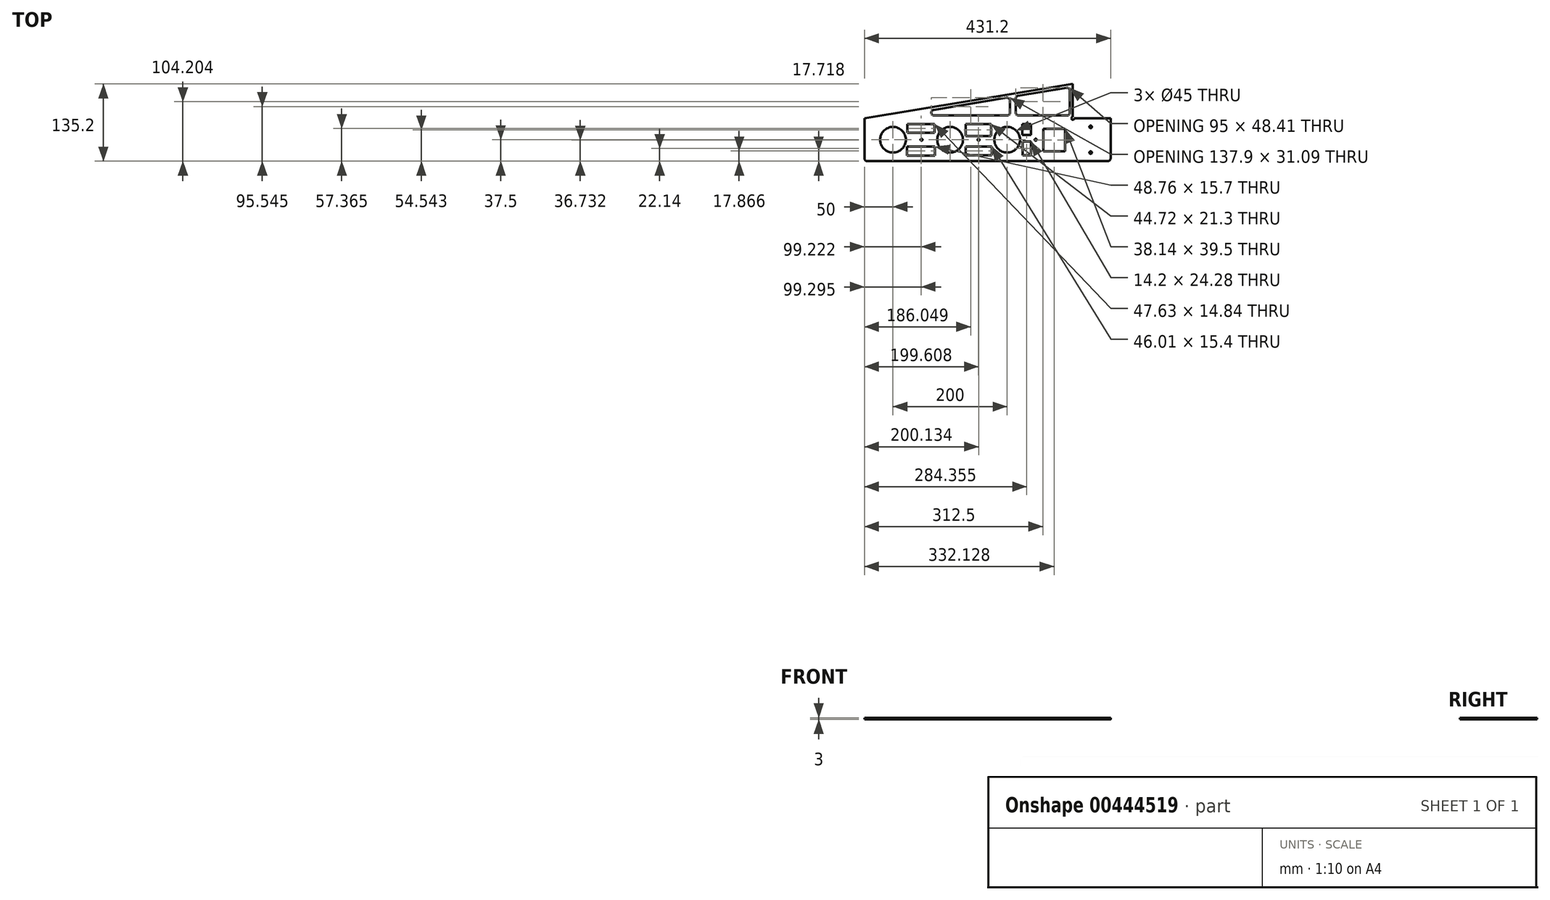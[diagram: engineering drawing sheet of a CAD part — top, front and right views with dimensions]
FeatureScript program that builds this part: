
annotation { "Feature Type Name" : "Feature", "Feature Type Description" : "" }
export const myFeature = defineFeature(function(context is Context, id is Id, definition is map)
    precondition{}
    {
        {
            var Q0;
            Q0=qCreatedBy(makeId("Top.planeOp"),FACE);
            var sketch = newSketch(context, id + "F0", { "sketchPlane" : qUnion([Q0])});
            skLineSegment(sketch, "E0.bottom", {"start": v(5, 0) * mm, "end": v(426.2, 0) * mm});
            skLineSegment(sketch, "E0.top", {"start": v(0, 75) * mm, "end": v(431.2, 75) * mm});
            skLineSegment(sketch, "E0.left", {"start": v(0, 5) * mm, "end": v(0, 75) * mm});
            skLineSegment(sketch, "E0.right", {"start": v(431.2, 5) * mm, "end": v(431.2, 75) * mm});
            skLineSegment(sketch, "E1", {"start": v(0, 75) * mm, "end": v(365, 135.2) * mm});
            skLineSegment(sketch, "E2", {"start": v(365, 135.2) * mm, "end": v(365, 75) * mm});
            skPoint(sketch, "E2.endSnap0", {"position": v(215.6, 75) * mm});
            skCircle(sketch, "E3", {"center": v(365, 75) * mm, "radius": 2.5 * mm});
            skCircle(sketch, "E4", {"center": v(100, 37.5) * mm, "radius": 1.75 * mm});
            skPoint(sketch, "E4.centerSnap0", {"position": v(0, 37.5) * mm});
            skCircle(sketch, "E5", {"center": v(200, 37.5) * mm, "radius": 1.75 * mm});
            skCircle(sketch, "E6", {"center": v(300, 37.5) * mm, "radius": 1.75 * mm});
            skCircle(sketch, "E7", {"center": v(396.2, 60) * mm, "radius": 2.25 * mm});
            skCircle(sketch, "E8", {"center": v(396.2, 15) * mm, "radius": 2.25 * mm});
            skLineSegment(sketch, "E9.0", {"start": v(360, 123.42) * mm, "end": v(360, 85) * mm});
            skLineSegment(sketch, "E10.0", {"start": v(122.08, 80) * mm, "end": v(250, 80) * mm});
            skLineSegment(sketch, "E10.1", {"start": v(121.27, 89.93) * mm, "end": v(249.19, 111.03) * mm});
            skPoint(sketch, "E11.visualSharp", {"position": v(360, 129.3) * mm});
            skArc(sketch, "E11.filletArc", {"start": v(360, 123.42) * mm, "mid": v(358.24, 127.23) * mm, "end": v(354.19, 128.35) * mm});
            skArc(sketch, "E12.filletArc", {"start": v(355, 80) * mm, "mid": v(358.54, 81.46) * mm, "end": v(360, 85) * mm});
            skPoint(sketch, "E13.visualSharp", {"position": v(61.04, 80) * mm});
            skArc(sketch, "E13.filletArc", {"start": v(121.27, 89.93) * mm, "mid": v(117.1, 84.6) * mm, "end": v(122.08, 80) * mm});
            skLineSegment(sketch, "E14.0", {"start": v(265, 85) * mm, "end": v(265, 109.4) * mm});
            skLineSegment(sketch, "E15.0", {"start": v(255, 85) * mm, "end": v(255, 106.1) * mm});
            skLineSegment(sketch, "E16.trimOffspring", {"start": v(270, 80) * mm, "end": v(355, 80) * mm});
            skLineSegment(sketch, "E17.trimOffspring", {"start": v(269.19, 114.33) * mm, "end": v(354.19, 128.35) * mm});
            skPoint(sketch, "E18.visualSharp", {"position": v(255, 111.99) * mm});
            skArc(sketch, "E18.filletArc", {"start": v(255, 106.1) * mm, "mid": v(253.24, 109.91) * mm, "end": v(249.19, 111.03) * mm});
            skPoint(sketch, "E19.visualSharp", {"position": v(255, 80) * mm});
            skArc(sketch, "E19.filletArc", {"start": v(250, 80) * mm, "mid": v(253.54, 81.46) * mm, "end": v(255, 85) * mm});
            skPoint(sketch, "E20.visualSharp", {"position": v(265, 113.64) * mm});
            skArc(sketch, "E20.filletArc", {"start": v(269.19, 114.33) * mm, "mid": v(266.19, 112.63) * mm, "end": v(265, 109.4) * mm});
            skPoint(sketch, "E21.visualSharp", {"position": v(265, 80) * mm});
            skArc(sketch, "E21.filletArc", {"start": v(265, 85) * mm, "mid": v(266.46, 81.46) * mm, "end": v(270, 80) * mm});
            skCircle(sketch, "E22", {"center": v(50, 37.5) * mm, "radius": 22.5 * mm});
            skCircle(sketch, "E23.1.0.0", {"center": v(150, 37.5) * mm, "radius": 22.5 * mm});
            skCircle(sketch, "E23.2.0.0", {"center": v(250, 37.5) * mm, "radius": 22.5 * mm});
            skLineSegment(sketch, "E23.direction1", {"start": v(50, 37.5) * mm, "end": v(150, 37.5) * mm, "construction": true});
            skPoint(sketch, "E24.visualSharp", {"position": v(0, 0) * mm});
            skArc(sketch, "E24.filletArc", {"start": v(0, 5) * mm, "mid": v(1.46, 1.46) * mm, "end": v(5, 0) * mm});
            skPoint(sketch, "E25.visualSharp", {"position": v(431.2, 0) * mm});
            skArc(sketch, "E25.filletArc", {"start": v(426.2, 0) * mm, "mid": v(429.74, 1.46) * mm, "end": v(431.2, 5) * mm});
            skLineSegment(sketch, "E26.0", {"start": v(10, 15) * mm, "end": v(10, 60) * mm});
            skLineSegment(sketch, "E27.0", {"start": v(15, 10) * mm, "end": v(346.2, 10) * mm});
            skLineSegment(sketch, "E28.0", {"start": v(351.2, 15) * mm, "end": v(351.2, 60) * mm});
            skLineSegment(sketch, "E29.0", {"start": v(15, 65) * mm, "end": v(346.2, 65) * mm});
            skPoint(sketch, "E30.visualSharp", {"position": v(10, 10) * mm});
            skArc(sketch, "E30.filletArc", {"start": v(10, 15) * mm, "mid": v(11.46, 11.46) * mm, "end": v(15, 10) * mm});
            skPoint(sketch, "E31.visualSharp", {"position": v(10, 65) * mm});
            skArc(sketch, "E31.filletArc", {"start": v(15, 65) * mm, "mid": v(11.46, 63.54) * mm, "end": v(10, 60) * mm});
            skPoint(sketch, "E32.visualSharp", {"position": v(351.2, 65) * mm});
            skArc(sketch, "E32.filletArc", {"start": v(351.2, 60) * mm, "mid": v(349.74, 63.54) * mm, "end": v(346.2, 65) * mm});
            skPoint(sketch, "E33.visualSharp", {"position": v(351.2, 10) * mm});
            skArc(sketch, "E33.filletArc", {"start": v(346.2, 10) * mm, "mid": v(349.74, 11.46) * mm, "end": v(351.2, 15) * mm});
            skLineSegment(sketch, "E34.bottom", {"start": v(74.84, 9.87) * mm, "end": v(123.6, 9.87) * mm});
            skLineSegment(sketch, "E34.top", {"start": v(74.84, 25.57) * mm, "end": v(123.6, 25.57) * mm});
            skLineSegment(sketch, "E34.left", {"start": v(74.84, 9.87) * mm, "end": v(74.84, 25.57) * mm});
            skLineSegment(sketch, "E34.right", {"start": v(123.6, 9.87) * mm, "end": v(123.6, 25.57) * mm});
            skLineSegment(sketch, "E35.bottom", {"start": v(177.13, 10.17) * mm, "end": v(223.14, 10.17) * mm});
            skLineSegment(sketch, "E35.top", {"start": v(177.13, 25.57) * mm, "end": v(223.14, 25.57) * mm});
            skLineSegment(sketch, "E35.left", {"start": v(177.13, 10.17) * mm, "end": v(177.13, 25.57) * mm});
            skLineSegment(sketch, "E35.right", {"start": v(223.14, 10.17) * mm, "end": v(223.14, 25.57) * mm});
            skLineSegment(sketch, "E36.bottom", {"start": v(75.48, 64.79) * mm, "end": v(123.11, 64.79) * mm});
            skLineSegment(sketch, "E36.top", {"start": v(75.48, 49.94) * mm, "end": v(123.11, 49.94) * mm});
            skLineSegment(sketch, "E36.left", {"start": v(75.48, 64.79) * mm, "end": v(75.48, 49.94) * mm});
            skLineSegment(sketch, "E36.right", {"start": v(123.11, 64.79) * mm, "end": v(123.11, 49.94) * mm});
            skLineSegment(sketch, "E37.bottom", {"start": v(177.25, 43.9) * mm, "end": v(221.97, 43.9) * mm});
            skLineSegment(sketch, "E37.top", {"start": v(177.25, 65.2) * mm, "end": v(221.97, 65.2) * mm});
            skLineSegment(sketch, "E37.left", {"start": v(177.25, 43.9) * mm, "end": v(177.25, 65.2) * mm});
            skLineSegment(sketch, "E37.right", {"start": v(221.97, 43.9) * mm, "end": v(221.97, 65.2) * mm});
            skLineSegment(sketch, "E38.bottom", {"start": v(313.06, 56.48) * mm, "end": v(351.2, 56.48) * mm});
            skLineSegment(sketch, "E38.top", {"start": v(313.06, 16.98) * mm, "end": v(351.2, 16.98) * mm});
            skLineSegment(sketch, "E38.left", {"start": v(313.06, 56.48) * mm, "end": v(313.06, 16.98) * mm});
            skLineSegment(sketch, "E38.right", {"start": v(351.2, 56.48) * mm, "end": v(351.2, 16.98) * mm});
            skLineSegment(sketch, "E39.bottom", {"start": v(291.46, 34.28) * mm, "end": v(277.25, 34.28) * mm});
            skLineSegment(sketch, "E39.top", {"start": v(291.46, 10) * mm, "end": v(277.25, 10) * mm});
            skLineSegment(sketch, "E39.left", {"start": v(291.46, 34.28) * mm, "end": v(291.46, 10) * mm});
            skLineSegment(sketch, "E39.right", {"start": v(277.25, 34.28) * mm, "end": v(277.25, 10) * mm});
            skLineSegment(sketch, "E40.bottom", {"start": v(291.46, 46) * mm, "end": v(276.67, 46) * mm});
            skLineSegment(sketch, "E40.top", {"start": v(291.46, 65) * mm, "end": v(276.67, 65) * mm});
            skLineSegment(sketch, "E40.left", {"start": v(291.46, 46) * mm, "end": v(291.46, 65) * mm});
            skLineSegment(sketch, "E40.right", {"start": v(276.67, 46) * mm, "end": v(276.67, 65) * mm});
            skSolve(sketch);
        }
        {
            var Q0;
            {var subQ0=sQuery(id+"F0.wireOp",EDGE,"E1");Q0=makeQuery(id+"F0.imprint","IMPRINT",FACE,{"disambiguationData":[TD([[makeQuery(id+"F0.imprint","IMPRINT",EDGE,{"derivedFrom":subQ0}),-1.0]])]});}
            var Q1;
            Q1=makeQuery(id+"F0.imprint","IMPRINT",FACE,{"disambiguationData":[TD([[makeQuery(id+"F0.imprint","IMPRINT",EDGE,{"derivedFrom":sQuery(id+"F0.wireOp",EDGE,"E0.bottom")}),1.0]])]});
            var Q2;
            Q2=makeQuery(id+"F0.imprint","IMPRINT",FACE,{"disambiguationData":[TD([[makeQuery(id+"F0.imprint","IMPRINT",EDGE,{"derivedFrom":sQuery(id+"F0.wireOp",EDGE,"E4")}),-1.0]])]});
            extrude(context, id + "F1", {"entities" : qUnion([Q0, Q1, Q2]), "depth" : 3 * mm});
        }
    });
